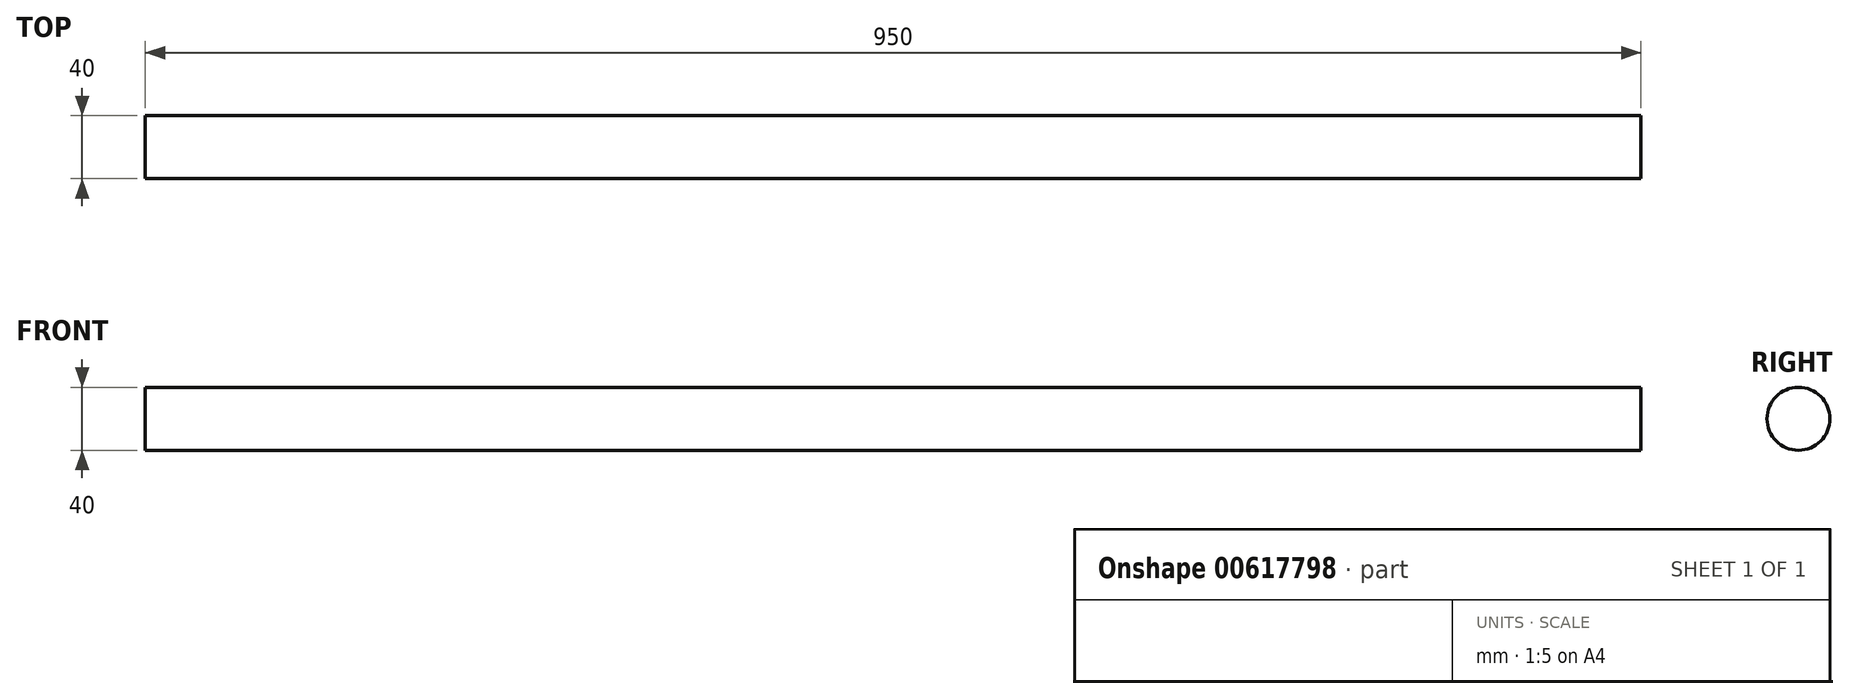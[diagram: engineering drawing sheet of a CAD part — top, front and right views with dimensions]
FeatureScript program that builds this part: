
annotation { "Feature Type Name" : "Feature", "Feature Type Description" : "" }
export const myFeature = defineFeature(function(context is Context, id is Id, definition is map)
    precondition{}
    {
        {
            var Q0;
            Q0=qCreatedBy(makeId("Right.planeOp"),FACE);
            var sketch = newSketch(context, id + "F0", { "sketchPlane" : qUnion([Q0])});
            skCircle(sketch, "E0", {"center": v(0, 0) * mm, "radius": 20 * mm});
            skSolve(sketch);
        }
        {
            var Q0;
            Q0=makeQuery(id+"F0.imprint","IMPRINT",FACE,{"disambiguationData":[TD([[makeQuery(id+"F0.imprint","IMPRINT",EDGE,{"derivedFrom":sQuery(id+"F0.wireOp",EDGE,"E0")}),1.0]])]});
            extrude(context, id + "F1", {"entities" : qUnion([Q0]), "depth" : 950 * mm, "offsetDistance" : 25 * mm});
        }
    });
